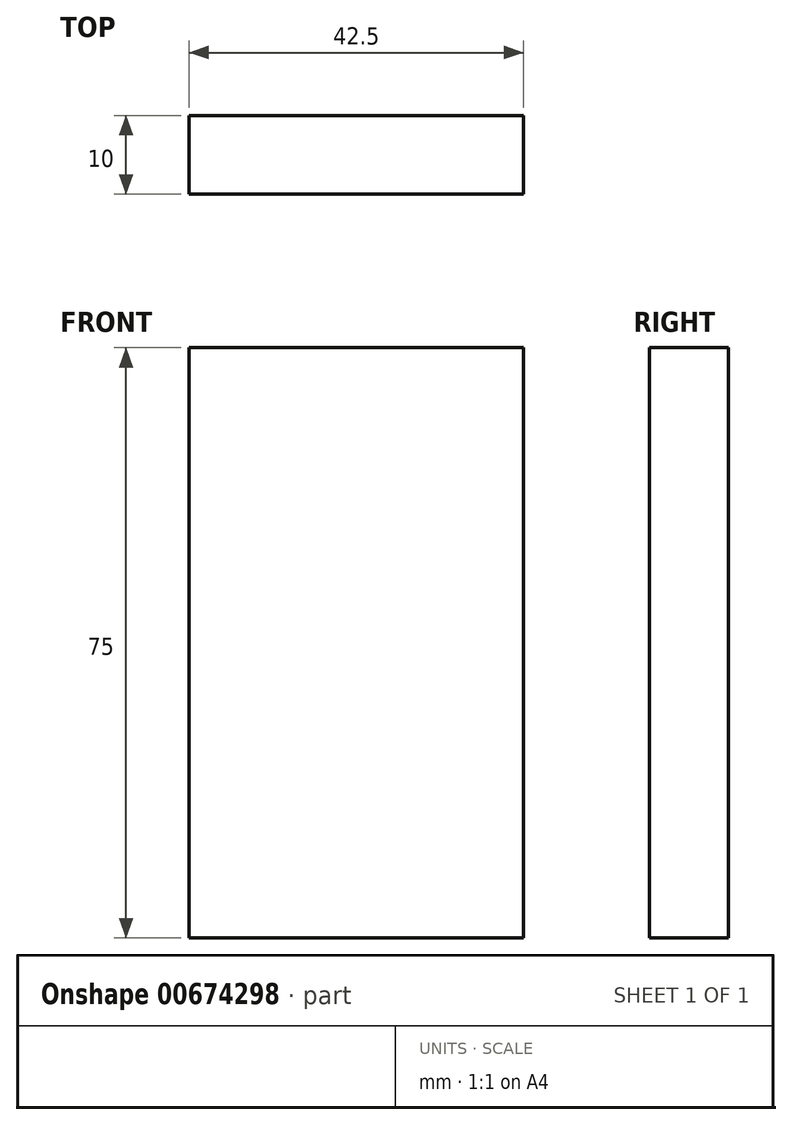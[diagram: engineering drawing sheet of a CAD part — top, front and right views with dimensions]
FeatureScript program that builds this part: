
annotation { "Feature Type Name" : "Feature", "Feature Type Description" : "" }
export const myFeature = defineFeature(function(context is Context, id is Id, definition is map)
    precondition{}
    {
        {
            var Q0;
            Q0=qCreatedBy(makeId("Front.planeOp"),FACE);
            var sketch = newSketch(context, id + "F0", { "sketchPlane" : qUnion([Q0])});
            skLineSegment(sketch, "E0.bottom", {"start": v(-21.1, 41.65) * mm, "end": v(21.4, 41.65) * mm});
            skLineSegment(sketch, "E0.top", {"start": v(-21.1, -33.35) * mm, "end": v(21.4, -33.35) * mm});
            skLineSegment(sketch, "E0.left", {"start": v(-21.1, 41.65) * mm, "end": v(-21.1, -33.35) * mm});
            skLineSegment(sketch, "E0.right", {"start": v(21.4, 41.65) * mm, "end": v(21.4, -33.35) * mm});
            skSolve(sketch);
        }
        {
            var Q0;
            Q0 = qSketchRegion(id + "F0", true);
            extrude(context, id + "F1", {"entities" : qUnion([Q0]), "depth" : 10 * mm, "offsetDistance" : 25 * mm});
        }
    });
